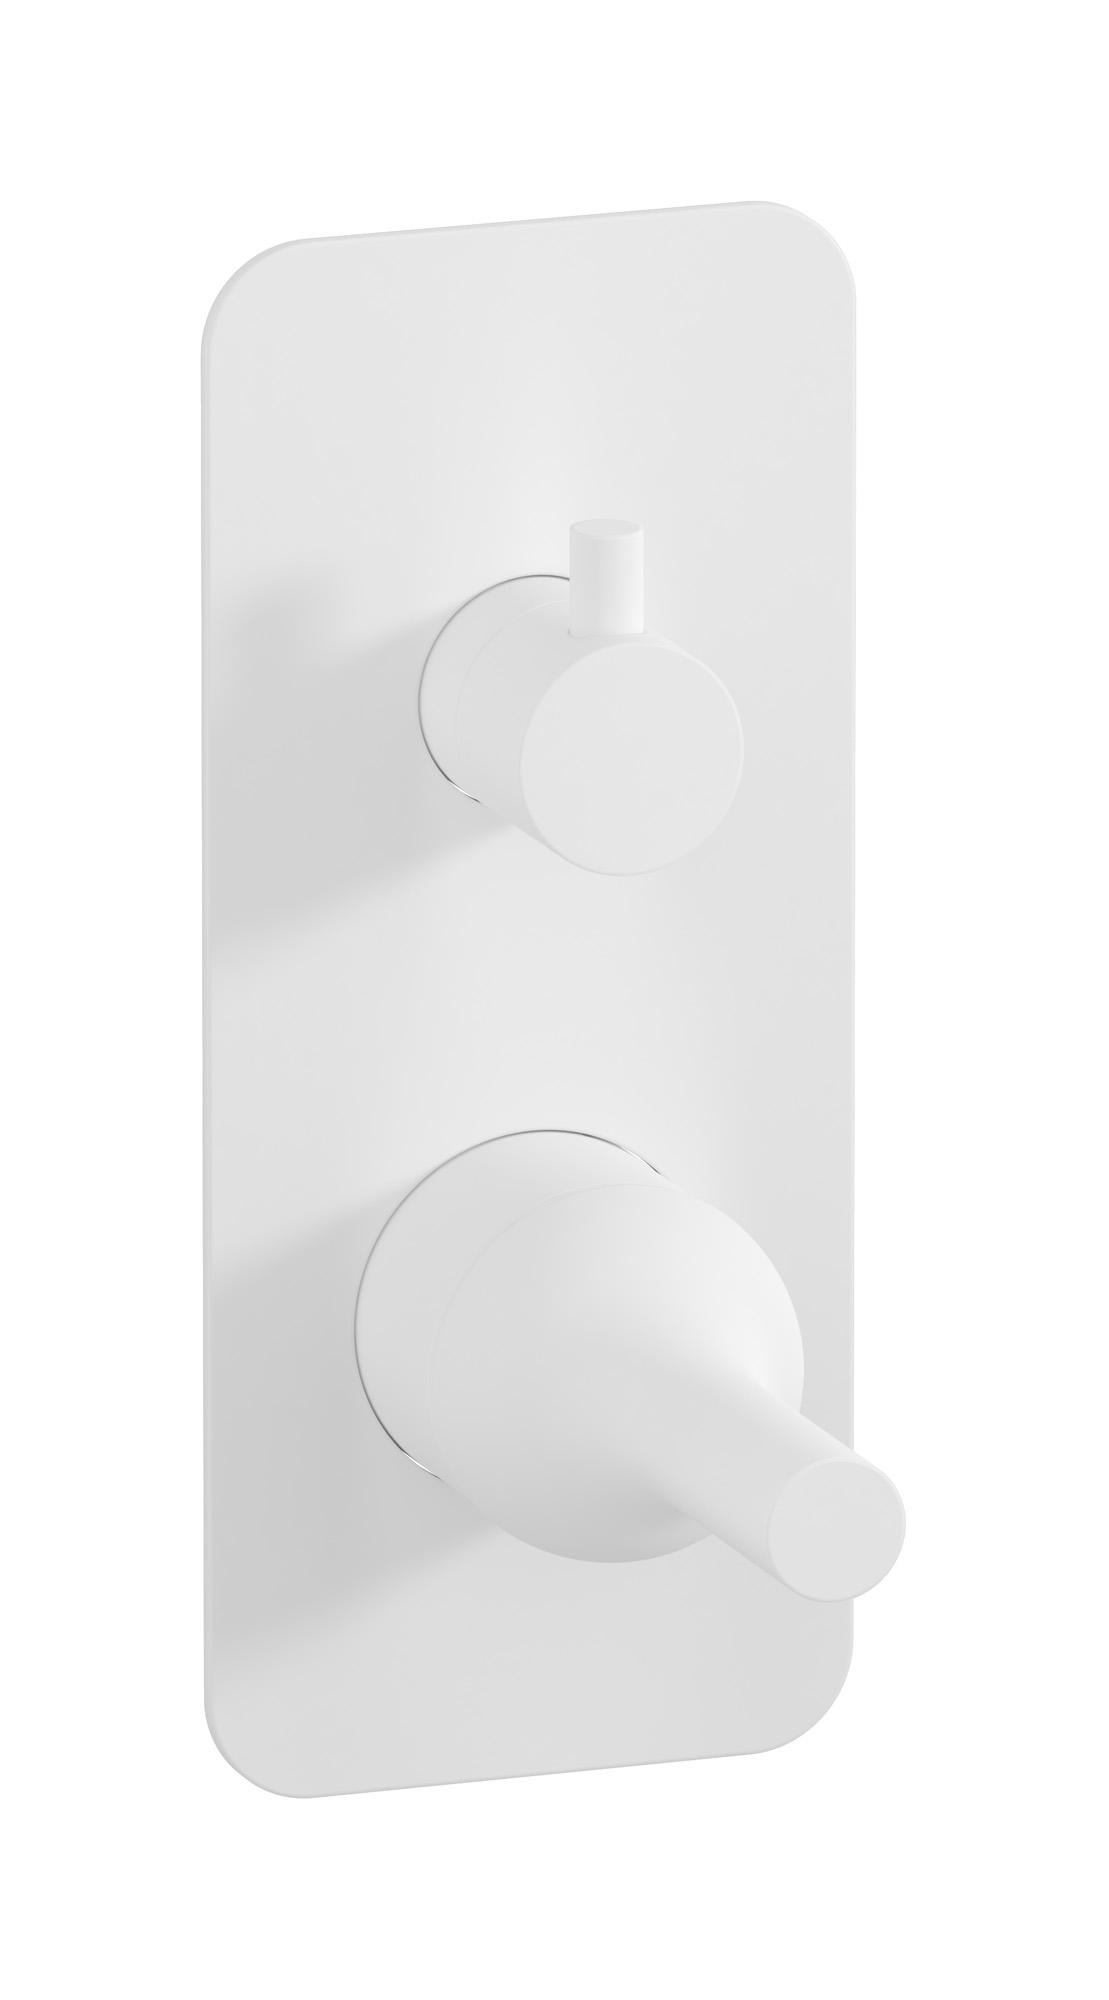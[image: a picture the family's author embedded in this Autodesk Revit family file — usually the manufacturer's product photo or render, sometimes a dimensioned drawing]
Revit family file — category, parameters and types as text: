
# Revit family: BI310
name_source: partatom
category: Apparecchi idraulici
units: mm (PartAtom-declared; Revit-internal decimal feet)

## family parameters
Basato su piano di lavoro = No
Condiviso = No
Mantieni orientamento annotazione = No
Numero OmniClass = 23.45.55.17
Punto di calcolo locali = No
Quota connettore circolare = Usa diametro
Sempre verticale = Sì
Taglio con vuoti quando caricato = No
Tipo di parte = Normale
Titolo OmniClass = Mixing Faucets

## types (4) — shared parameters
Cold water inlet = 10 mm  [stored 0.0328084 ft]
Commenti sul tipo = Exposed parts for manual wall mixer with two ways diverter
Connessione CW = No
Connessione HW = No
Connessione di scarico = No
Connessione di ventilazione = No
Descrizione = Exposed parts for manual wall mixer with two ways diverter
Hot water inlet = 10 mm  [stored 0.0328084 ft]
Produttore = IB Rubinetterie S.p.A.
URL = https://www.weareib.it
zero-valued in all types: Prospetto di default

## per-type parameters (varying)
| type | Finishes surface | Immagine tipo | Modello |
| Chrome | IB_Chrome | BI310CC.jpg | BI310CC |
| Brushed nickel | IB_Brushed nickel | BI310SS.jpg | BI310SS |
| Matt black | IB_matt black | BI310NP.jpg | BI310NP |
| Matt white | IB_matt white | BI310BO.jpg | BI310BO |

note: [stored X ft] marks values corroborated as IEEE doubles in the binary element streams (Revit-internal decimal feet)
